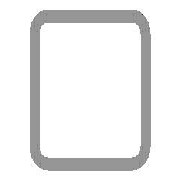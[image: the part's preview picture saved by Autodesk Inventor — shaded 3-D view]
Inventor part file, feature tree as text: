
AUTODESK INVENTOR PART (.ipt)
format: ipt  version: 2016 (Build 200138000, 138)  size: 132,608 bytes
history: native  units: mm (DEFAULTED — no unit token found)
features: other x4, sketch x3, plane x2, split x1
ambient origin geometry x8: Origin, YZ Plane, XZ Plane, XY Plane, X Axis, Y Axis, Z Axis, Center Point
bodies: Solid1 (feature_tree), Body (feature_tree)
feature tree (10):
  parser-record x1  (decoder bookkeeping rows leaked as tree rows — omitted from the tree; the rows remain in map.json)
  other  "Driven Length"
  other  "Start plane"
  other  "End plane"
  plane  "Work Plane4"
  split  "Split1"
  sketch  "Sketch"  dims[d7=4.0mm d9=25.0mm d11=25.0mm d12=2.0mm d13=-0.0mm d14=275.0mm d15=12.5mm d16=12.5mm d17=90.0deg d18=275.0mm]
  sketch  "Sketch3"  dims[d3=275.0mm]
  plane  "Work Plane3"
  sketch  "Sketch4"  dims[d4=0.0mm]
